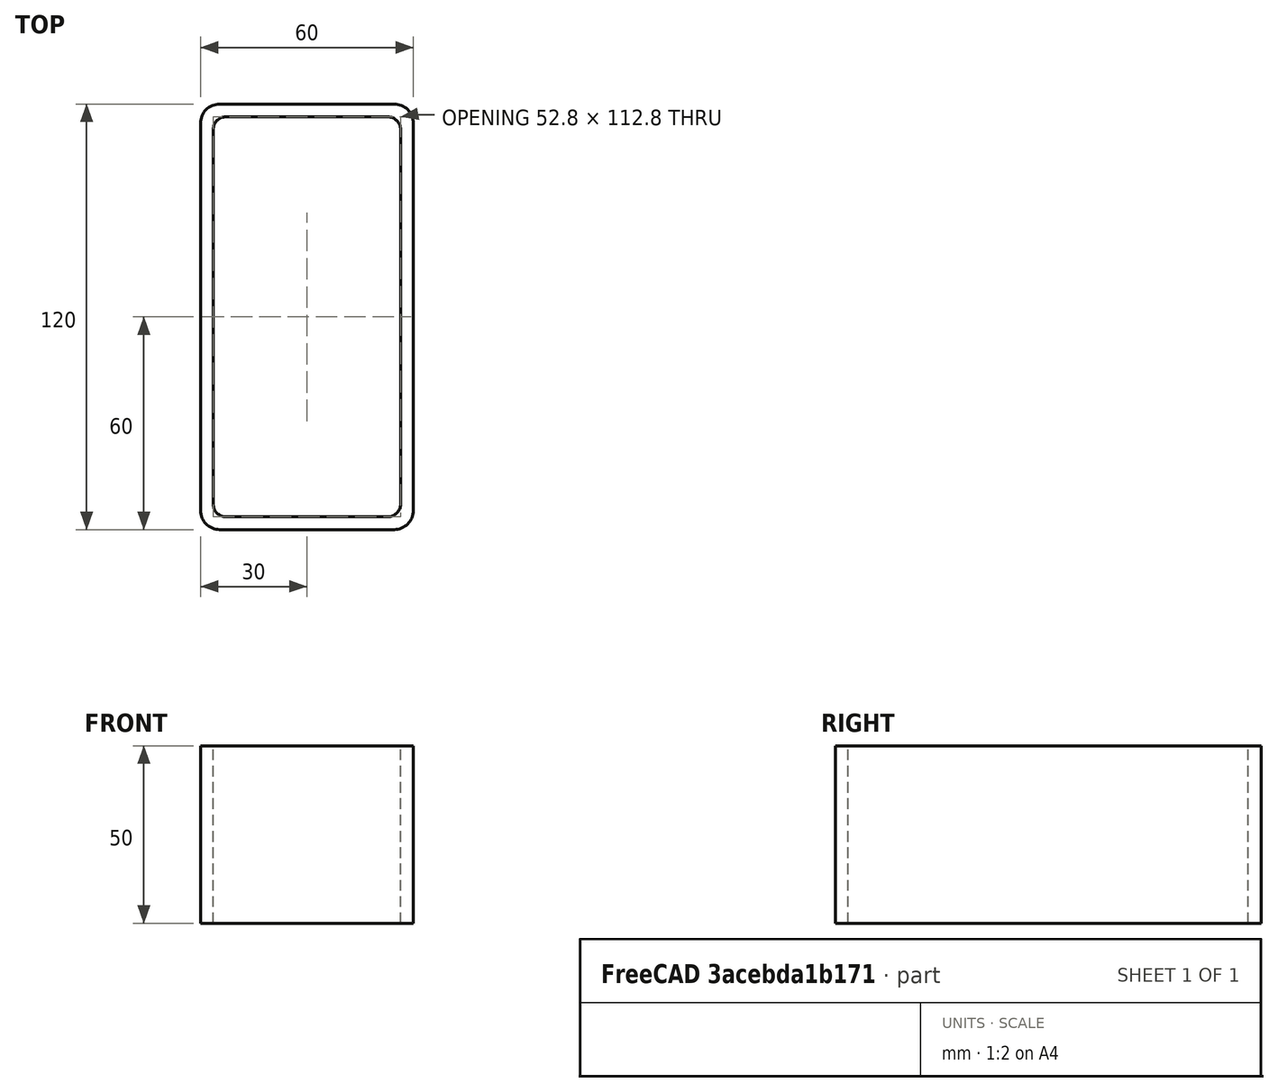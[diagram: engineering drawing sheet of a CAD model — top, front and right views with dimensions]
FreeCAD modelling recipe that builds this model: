
FCSTD DOCUMENT  (FreeCAD 0.15R4671 (Git))
Label: Rectangular hollow section 120x60x3.6 EN10219 S235JRH
License: All rights reserved
LicenseURL: http://en.wikipedia.org/wiki/All_rights_reserved
objects: Sketcher::SketchObject×1, Part::Extrusion×1
note: 2 computed .brp shape members not serialized (recipe doc carries the construction recipe); baked Part::Feature solids carry a one-line shape summary decoded from their .brp

FEATURE [Sketcher::SketchObject] Sketch
  sketch-geometry (16):
    g0: LineSegment StartX=-22.8 StartY=56.4 StartZ=0 EndX=22.8 EndY=56.4 EndZ=0
    g1: LineSegment StartX=26.4 StartY=52.8 StartZ=0 EndX=26.4 EndY=-52.8 EndZ=0
    g2: LineSegment StartX=22.8 StartY=-56.4 StartZ=0 EndX=-22.8 EndY=-56.4 EndZ=0
    g3: LineSegment StartX=-26.4 StartY=-52.8 StartZ=0 EndX=-26.4 EndY=52.8 EndZ=0
    g4: LineSegment StartX=-24.6 StartY=60 StartZ=0 EndX=24.6 EndY=60 EndZ=0
    g5: LineSegment StartX=30 StartY=54.6 StartZ=0 EndX=30 EndY=-54.6 EndZ=0
    g6: LineSegment StartX=24.6 StartY=-60 StartZ=0 EndX=-24.6 EndY=-60 EndZ=0
    g7: LineSegment StartX=-30 StartY=-54.6 StartZ=0 EndX=-30 EndY=54.6 EndZ=0
    g8: ArcOfCircle CenterX=-22.8 CenterY=52.8 CenterZ=0 NormalX=0 NormalY=0 NormalZ=1 Radius=3.6 StartAngle=1.5708 EndAngle=3.14159
    g9: ArcOfCircle CenterX=22.8 CenterY=52.8 CenterZ=0 NormalX=0 NormalY=0 NormalZ=1 Radius=3.6 StartAngle=0 EndAngle=1.5708
    g10: ArcOfCircle CenterX=22.8 CenterY=-52.8 CenterZ=0 NormalX=0 NormalY=0 NormalZ=1 Radius=3.6 StartAngle=4.71239 EndAngle=6.28319
    g11: ArcOfCircle CenterX=-22.8 CenterY=-52.8 CenterZ=0 NormalX=0 NormalY=0 NormalZ=1 Radius=3.6 StartAngle=3.14159 EndAngle=4.71239
    g12: ArcOfCircle CenterX=24.6 CenterY=54.6 CenterZ=0 NormalX=0 NormalY=0 NormalZ=1 Radius=5.4 StartAngle=0 EndAngle=1.5708
    g13: ArcOfCircle CenterX=24.6 CenterY=-54.6 CenterZ=0 NormalX=0 NormalY=0 NormalZ=1 Radius=5.4 StartAngle=4.71239 EndAngle=6.28319
    g14: ArcOfCircle CenterX=-24.6 CenterY=-54.6 CenterZ=0 NormalX=0 NormalY=0 NormalZ=1 Radius=5.4 StartAngle=3.14159 EndAngle=4.71239
    g15: ArcOfCircle CenterX=-24.6 CenterY=54.6 CenterZ=0 NormalX=0 NormalY=0 NormalZ=1 Radius=5.4 StartAngle=1.5708 EndAngle=3.14159
  constraints (36):
    c: Horizontal(g2)
    c: Vertical(g3)
    c: Horizontal(g6)
    c: Vertical(g7)
    c: Tangent(g3,g8) = 1.5708
    c: Tangent(g0,g8) = 1.5708
    c: Tangent(g0,g9) = 1.5708
    c: Tangent(g1,g9) = 1.5708
    c: Tangent(g1,g10) = 1.5708
    c: Tangent(g2,g10) = 1.5708
    c: Tangent(g2,g11) = 1.5708
    c: Tangent(g3,g11) = 1.5708
    c: Tangent(g4,g12) = 1.5708
    c: Tangent(g5,g12) = 1.5708
    c: Tangent(g5,g13) = 1.5708
    c: Tangent(g6,g13) = 1.5708
    c: Tangent(g6,g14) = 1.5708
    c: Tangent(g7,g14) = 1.5708
    c: Tangent(g7,g15) = 1.5708
    c: Tangent(g4,g15) = 1.5708
    c: Equal(g9,g8)
    c: Equal(g9,g11)
    c: Equal(g9,g10)
    c: Equal(g12,g15)
    c: Equal(g12,g14)
    c: Equal(g12,g13)
    c: Symmetric(g4,g6,g-1)
    c: Symmetric(g7,g5,g-2)
    c: DistanceY(g4,g6) = -120
    c: DistanceX(g7,g5) = 60
    c: Symmetric(g3,g1,g-2)
    c: Symmetric(g0,g2,g-1)
    c: DistanceY(g0,g4) = 3.6
    c: DistanceX(g5,g1) = -3.6
    c: Radius(g9) = 3.6
    c: Radius(g12) = 5.4
FEATURE [Part::Extrusion] Extrude  label="Rectangular hollow section 120x60x3.6 EN10219 S235JRH"
  Base = -> Sketch
  Dir = (0,0,50)
  Solid = true
